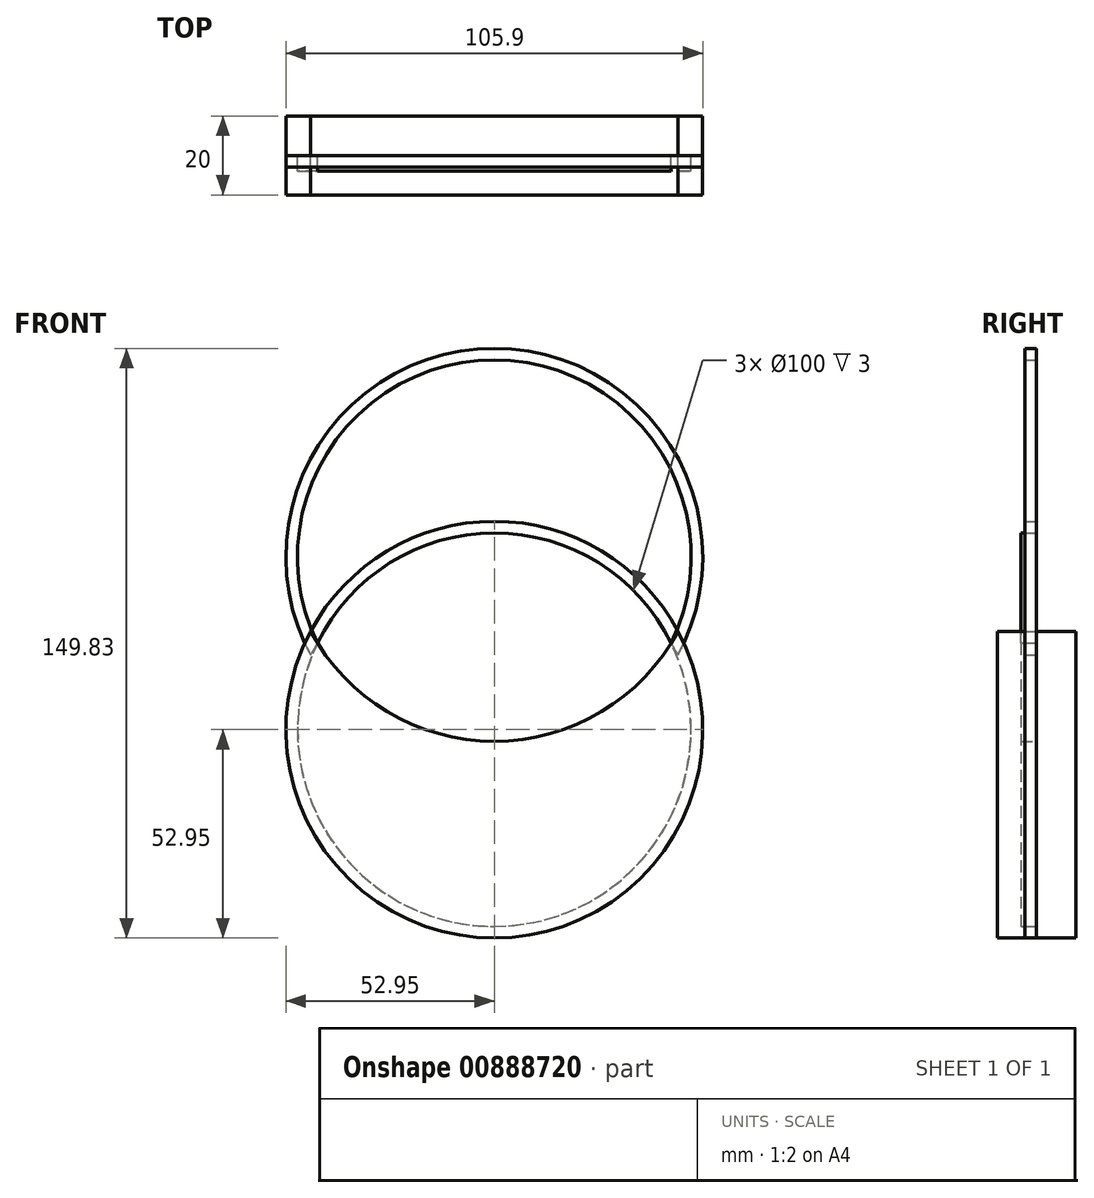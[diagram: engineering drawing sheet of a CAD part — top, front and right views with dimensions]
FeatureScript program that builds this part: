
annotation { "Feature Type Name" : "Feature", "Feature Type Description" : "" }
export const myFeature = defineFeature(function(context is Context, id is Id, definition is map)
    precondition{}
    {
        {
            var Q0;
            Q0=qCreatedBy(makeId("Front.planeOp"),FACE);
            var sketch = newSketch(context, id + "F0", { "sketchPlane" : qUnion([Q0])});
            skCircle(sketch, "E0", {"center": v(0, 0) * mm, "radius": 50 * mm});
            skCircle(sketch, "E1", {"center": v(0, 0) * mm, "radius": 52.95 * mm});
            skLineSegment(sketch, "E2", {"start": v(0, 0) * mm, "end": v(0, 50) * mm, "construction": true});
            skCircle(sketch, "E3", {"center": v(0, 50) * mm, "radius": 52.95 * mm});
            skSolve(sketch);
        }
        {
            var Q0;
            Q0=makeQuery(id+"F0.imprint","IMPRINT",FACE,{"disambiguationData":[TD([[makeQuery(id+"F0.imprint","IMPRINT",EDGE,{"derivedFrom":sQuery(id+"F0.wireOp",EDGE,"E1")}),1.0]])]});
            extrude(context, id + "F1", {"entities" : qUnion([Q0]), "depth" : 3 * mm, "offsetDistance" : 25 * mm});
        }
        {
            var Q0;
            Q0=makeQuery(id+"F0.imprint","IMPRINT",FACE,{"disambiguationData":[TD([[makeQuery(id+"F0.imprint","IMPRINT",EDGE,{"derivedFrom":sQuery(id+"F0.wireOp",EDGE,"E0")}),1.0]])]});
            var Q1;
            Q1=sQuery(id+"F0.wireOp",EDGE,"E0");
            var Q2;
            Q2=sQuery(id+"F0.wireOp",EDGE,"E1");
            extrude(context, id + "F2", {"entities" : qUnion([Q0]), "surfaceEntities" : qUnion([Q1, Q2]), "depth" : 4 * mm, "offsetDistance" : 25 * mm});
        }
        {
            var Q0;
            {var subQ0=sQuery(id+"F0.wireOp",EDGE,"E3");var subQ1=sQuery(id+"F0.wireOp",EDGE,"E0");var subQ2=makeQuery(id+"F0.imprint","INTERSECT",VERTEX,{"disambiguationData":[OD(0.0)],"derivedFrom":[subQ1,subQ0]});Q0=makeQuery(id+"F0.imprint","IMPRINT",FACE,{"disambiguationData":[TD([[makeQuery(id+"F0.imprint","IMPRINT",EDGE,{"disambiguationData":[TD([[subQ2,1.0]])],"derivedFrom":subQ1}),1.0]])]});}
            var Q1;
            {var subQ0=sQuery(id+"F0.wireOp",EDGE,"E3");var subQ1=sQuery(id+"F0.wireOp",EDGE,"E0");var subQ2=makeQuery(id+"F0.imprint","INTERSECT",VERTEX,{"disambiguationData":[OD(0.0)],"derivedFrom":[subQ1,subQ0]});Q1=makeQuery(id+"F0.imprint","IMPRINT",FACE,{"disambiguationData":[TD([[makeQuery(id+"F0.imprint","IMPRINT",EDGE,{"disambiguationData":[TD([[subQ2,1.0]])],"derivedFrom":subQ1}),-1.0]])]});}
            extrude(context, id + "F3", {"entities" : qUnion([Q0, Q1]), "endBound" : BoundingType.SYMMETRIC, "depth" : 20 * mm, "offsetDistance" : 25 * mm});
        }
        {
            var Q0;
            Q0=makeQuery(id+"F3.opExtrude","SWEPT_BODY",BODY,{"disambiguationData":[OSD([sQuery(id+"F0.wireOp",EDGE,"E1"),sQuery(id+"F0.wireOp",EDGE,"E3")])]});
            var Q1;
            Q1=makeQuery(id+"F1.opExtrude","SWEPT_BODY",BODY,{"disambiguationData":[OSD([sQuery(id+"F0.wireOp",EDGE,"E0"),sQuery(id+"F0.wireOp",EDGE,"E1")])]});
            booleanBodies(context, id + "F4", {"operationType" : BooleanOperationType.INTERSECTION, "tools" : qUnion([Q0, Q1]), "keepTools" : true});
        }
        {
            var Q0;
            Q0=makeQuery(id+"F3.opExtrude","SWEPT_BODY",BODY,{"disambiguationData":[OSD([sQuery(id+"F0.wireOp",EDGE,"E1"),sQuery(id+"F0.wireOp",EDGE,"E3")])]});
            var Q1;
            Q1=makeQuery(id+"F2.opExtrude","SWEPT_BODY",BODY,{"disambiguationData":[OSD([sQuery(id+"F0.wireOp",EDGE,"E0")])]});
            booleanBodies(context, id + "F5", {"operationType" : BooleanOperationType.INTERSECTION, "tools" : qUnion([Q0, Q1]), "keepTools" : true});
        }
        {
            var Q0;
            Q0=makeQuery(id+"F5.opBoolean","INTERSECT",BODY,{"derivedFrom":[makeQuery(id+"F2.opExtrude","SWEPT_BODY",BODY,{"disambiguationData":[OSD([sQuery(id+"F0.wireOp",EDGE,"E0")])]}),makeQuery(id+"F3.opExtrude","SWEPT_BODY",BODY,{"disambiguationData":[OSD([sQuery(id+"F0.wireOp",EDGE,"E1"),sQuery(id+"F0.wireOp",EDGE,"E3")])]})]});
            var Q1;
            Q1=makeQuery(id+"F2.opExtrude","SWEPT_BODY",BODY,{"disambiguationData":[OSD([sQuery(id+"F0.wireOp",EDGE,"E0")])]});
            booleanBodies(context, id + "F6", {"operationType" : BooleanOperationType.SUBTRACTION, "tools" : qUnion([Q0]), "targets" : qUnion([Q1]), "keepTools" : true});
        }
        {
            var Q0;
            Q0=makeQuery(id+"F2.opExtrude","CAP_FACE",FACE,{"disambiguationData":[OSD([sQuery(id+"F0.wireOp",EDGE,"E0")])],"isStart":true});
            var sketch = newSketch(context, id + "F7", { "sketchPlane" : qUnion([Q0])});
            skLineSegment(sketch, "E4", {"start": v(-44.92, 21.97) * mm, "end": v(44.92, 21.97) * mm});
            skSolve(sketch);
        }
        {
            var Q0;
            Q0=sQuery(id+"F7.wireOp",EDGE,"E4");
            cPlane(context, id + "F8", {"entities" : qUnion([Q0]), "cplaneType" : CPlaneType.LINE_ANGLE, "offset" : 25 * mm, "angle" : 90 * degree, "width" : 150 * mm, "height" : 150 * mm});
        }
        {
            var Q0;
            {var subQ0=sQuery(id+"F0.wireOp",EDGE,"E1");Q0=makeQuery(id+"F4.opBoolean","INTERSECT",BODY,{"derivedFrom":[makeQuery(id+"F1.opExtrude","SWEPT_BODY",BODY,{"disambiguationData":[OSD([sQuery(id+"F0.wireOp",EDGE,"E0"),subQ0])]}),makeQuery(id+"F3.opExtrude","SWEPT_BODY",BODY,{"disambiguationData":[OSD([subQ0,sQuery(id+"F0.wireOp",EDGE,"E3")])]})]});}
            var Q1;
            Q1=qCreatedBy(id+"F8.planeOp",FACE);
            mirror(context, id + "F9", {"entities" : qUnion([Q0]), "mirrorPlane" : qUnion([Q1])});
        }
    });
